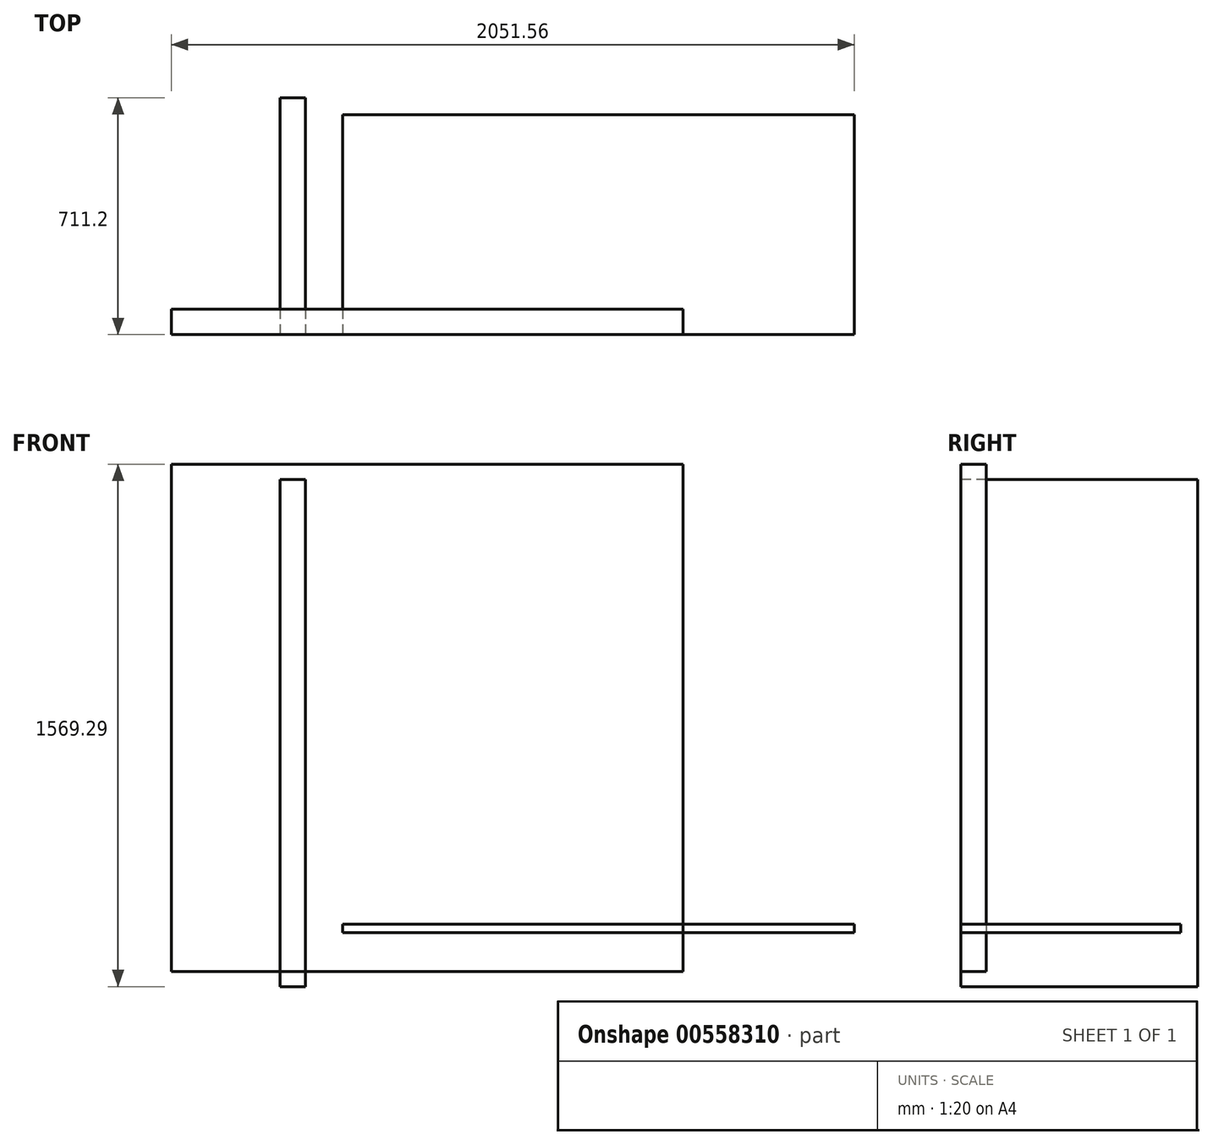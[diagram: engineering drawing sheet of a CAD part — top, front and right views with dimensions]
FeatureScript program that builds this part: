
annotation { "Feature Type Name" : "Feature", "Feature Type Description" : "" }
export const myFeature = defineFeature(function(context is Context, id is Id, definition is map)
    precondition{}
    {
        {
            var Q0;
            Q0=qCreatedBy(makeId("Front.planeOp"),FACE);
            var sketch = newSketch(context, id + "F0", { "sketchPlane" : qUnion([Q0])});
            skLineSegment(sketch, "E0.bottom", {"start": v(-97.75, 1326.37) * mm, "end": v(-21.55, 1326.37) * mm});
            skLineSegment(sketch, "E0.top", {"start": v(-97.75, -197.63) * mm, "end": v(-21.55, -197.63) * mm});
            skLineSegment(sketch, "E0.left", {"start": v(-97.75, 1326.37) * mm, "end": v(-97.75, -197.63) * mm});
            skLineSegment(sketch, "E0.right", {"start": v(-21.55, 1326.37) * mm, "end": v(-21.55, -197.63) * mm});
            skSolve(sketch);
        }
        {
            var Q0;
            Q0=qCreatedBy(makeId("Front.planeOp"),FACE);
            var sketch = newSketch(context, id + "F1", { "sketchPlane" : qUnion([Q0])});
            skLineSegment(sketch, "E1.bottom", {"start": v(91.29, -10.1) * mm, "end": v(1627.99, -10.1) * mm});
            skLineSegment(sketch, "E1.top", {"start": v(91.29, -35.5) * mm, "end": v(1627.99, -35.5) * mm});
            skLineSegment(sketch, "E1.left", {"start": v(91.29, -10.1) * mm, "end": v(91.29, -35.5) * mm});
            skLineSegment(sketch, "E1.right", {"start": v(1627.99, -10.1) * mm, "end": v(1627.99, -35.5) * mm});
            skSolve(sketch);
        }
        {
            var Q0;
            Q0=qCreatedBy(makeId("Front.planeOp"),FACE);
            var sketch = newSketch(context, id + "F2", { "sketchPlane" : qUnion([Q0])});
            skLineSegment(sketch, "E2.bottom", {"start": v(-423.57, 1371.66) * mm, "end": v(1113.13, 1371.66) * mm});
            skLineSegment(sketch, "E2.top", {"start": v(-423.57, -152.34) * mm, "end": v(1113.13, -152.34) * mm});
            skLineSegment(sketch, "E2.left", {"start": v(-423.57, 1371.66) * mm, "end": v(-423.57, -152.34) * mm});
            skLineSegment(sketch, "E2.right", {"start": v(1113.13, 1371.66) * mm, "end": v(1113.13, -152.34) * mm});
            skSolve(sketch);
        }
        {
            var Q0;
            Q0=makeQuery(id+"F0.imprint","IMPRINT",FACE,{"disambiguationData":[TD([[makeQuery(id+"F0.imprint","IMPRINT",EDGE,{"derivedFrom":sQuery(id+"F0.wireOp",EDGE,"E0.bottom")}),-1.0]])]});
            extrude(context, id + "F3", {"entities" : qUnion([Q0]), "depth" : -711.2 * mm, "offsetDistance" : 25.4 * mm});
        }
        {
            var Q0;
            Q0 = qSketchRegion(id + "F1", true);
            extrude(context, id + "F4", {"entities" : qUnion([Q0]), "depth" : -660.4 * mm, "offsetDistance" : 25.4 * mm});
        }
        {
            var Q0;
            Q0=makeQuery(id+"F2.imprint","IMPRINT",FACE,{"disambiguationData":[TD([[makeQuery(id+"F2.imprint","IMPRINT",EDGE,{"derivedFrom":sQuery(id+"F2.wireOp",EDGE,"E2.bottom")}),-1.0]])]});
            extrude(context, id + "F5", {"entities" : qUnion([Q0]), "depth" : -76.2 * mm, "offsetDistance" : 25.4 * mm});
        }
    });
